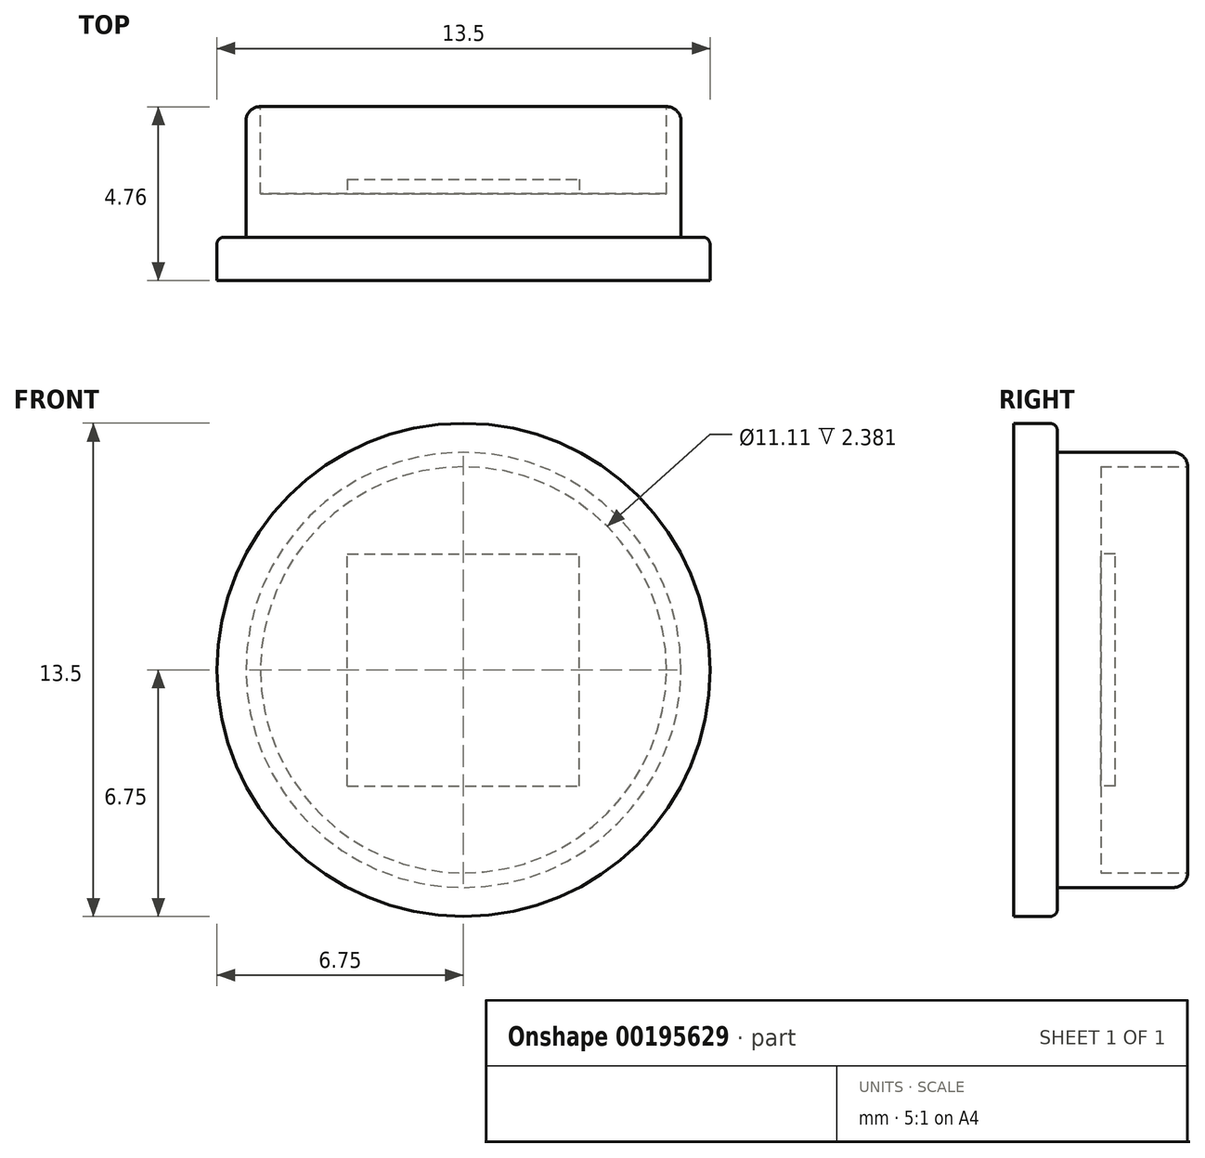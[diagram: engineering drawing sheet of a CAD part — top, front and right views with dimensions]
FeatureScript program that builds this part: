
annotation { "Feature Type Name" : "Feature", "Feature Type Description" : "" }
export const myFeature = defineFeature(function(context is Context, id is Id, definition is map)
    precondition{}
    {
        {
            var Q0;
            Q0=qCreatedBy(makeId("Front.planeOp"),FACE);
            var sketch = newSketch(context, id + "F0", { "sketchPlane" : qUnion([Q0])});
            skCircle(sketch, "E0", {"center": v(0, 0) * mm, "radius": 6.75 * mm});
            skSolve(sketch);
        }
        {
            var Q0;
            Q0 = qSketchRegion(id + "F0", true);
            extrude(context, id + "F1", {"entities" : qUnion([Q0]), "oppositeDirection" : true, "depth" : 1.2 * mm});
        }
        {
            var Q0;
            Q0=makeQuery(id+"F1.opExtrude","CAP_FACE",FACE,{"disambiguationData":[OSD([sQuery(id+"F0.wireOp",EDGE,"E0")])],"isStart":false});
            var sketch = newSketch(context, id + "F2", { "sketchPlane" : qUnion([Q0])});
            skCircle(sketch, "E1", {"center": v(0, 0) * mm, "radius": 5.95 * mm});
            skSolve(sketch);
        }
        {
            var Q0;
            Q0 = qSketchRegion(id + "F2", true);
            extrude(context, id + "F3", {"entities" : qUnion([Q0]), "operationType" : NewBodyOperationType.ADD, "depth" : 3.57 * mm});
        }
        {
            var Q0;
            Q0=makeQuery(id+"F3.opExtrude","CAP_EDGE",EDGE,{"disambiguationData":[OSD([sQuery(id+"F2.wireOp",EDGE,"E1")])],"isStart":false});
            fillet(context, id + "F4", {"entities" : qUnion([Q0]), "radius" : 0.4 * mm, "tangentPropagation" : true, "allowEdgeOverflow" : false});
        }
        {
            var Q0;
            Q0=makeQuery(id+"F3.opExtrude","CAP_EDGE",EDGE,{"disambiguationData":[OSD([sQuery(id+"F2.wireOp",EDGE,"E1")])],"isStart":true});
            var Q1;
            Q1=makeQuery(id+"F1.opExtrude","CAP_EDGE",EDGE,{"disambiguationData":[OSD([sQuery(id+"F0.wireOp",EDGE,"E0")])],"isStart":false});
            fillet(context, id + "F5", {"entities" : qUnion([Q0, Q1]), "radius" : 0.2 * mm, "tangentPropagation" : true, "allowEdgeOverflow" : false});
        }
        {
            var Q0;
            Q0=makeQuery(id+"F3.opExtrude","CAP_FACE",FACE,{"disambiguationData":[OSD([sQuery(id+"F2.wireOp",EDGE,"E1")])],"isStart":false});
            var sketch = newSketch(context, id + "F6", { "sketchPlane" : qUnion([Q0])});
            skCircle(sketch, "E2", {"center": v(0, 0) * mm, "radius": 5.56 * mm});
            skSolve(sketch);
        }
        {
            var Q0;
            Q0 = qSketchRegion(id + "F6", true);
            extrude(context, id + "F7", {"entities" : qUnion([Q0]), "operationType" : NewBodyOperationType.REMOVE, "oppositeDirection" : true, "depth" : 2.38 * mm});
        }
        {
            var Q0;
            Q0=makeQuery(id+"F7.boolean.opBoolean","COPY",FACE,{"derivedFrom":makeQuery(id+"F7.opExtrude","CAP_FACE",FACE,{"disambiguationData":[OSD([sQuery(id+"F6.wireOp",EDGE,"E2")])],"isStart":false})});
            var sketch = newSketch(context, id + "F8", { "sketchPlane" : qUnion([Q0])});
            skLineSegment(sketch, "E3.bottom", {"start": v(3.18, -3.17) * mm, "end": v(-3.17, -3.18) * mm});
            skLineSegment(sketch, "E3.top", {"start": v(3.17, 3.18) * mm, "end": v(-3.18, 3.18) * mm});
            skLineSegment(sketch, "E3.left", {"start": v(3.18, -3.17) * mm, "end": v(3.17, 3.18) * mm});
            skLineSegment(sketch, "E3.right", {"start": v(-3.17, -3.18) * mm, "end": v(-3.18, 3.18) * mm});
            skPoint(sketch, "E3.middle", {"position": v(0, 0) * mm});
            skSolve(sketch);
        }
        {
            var Q0;
            Q0 = qSketchRegion(id + "F8", true);
            extrude(context, id + "F9", {"entities" : qUnion([Q0]), "operationType" : NewBodyOperationType.ADD, "depth" : 0.4 * mm});
        }
    });
